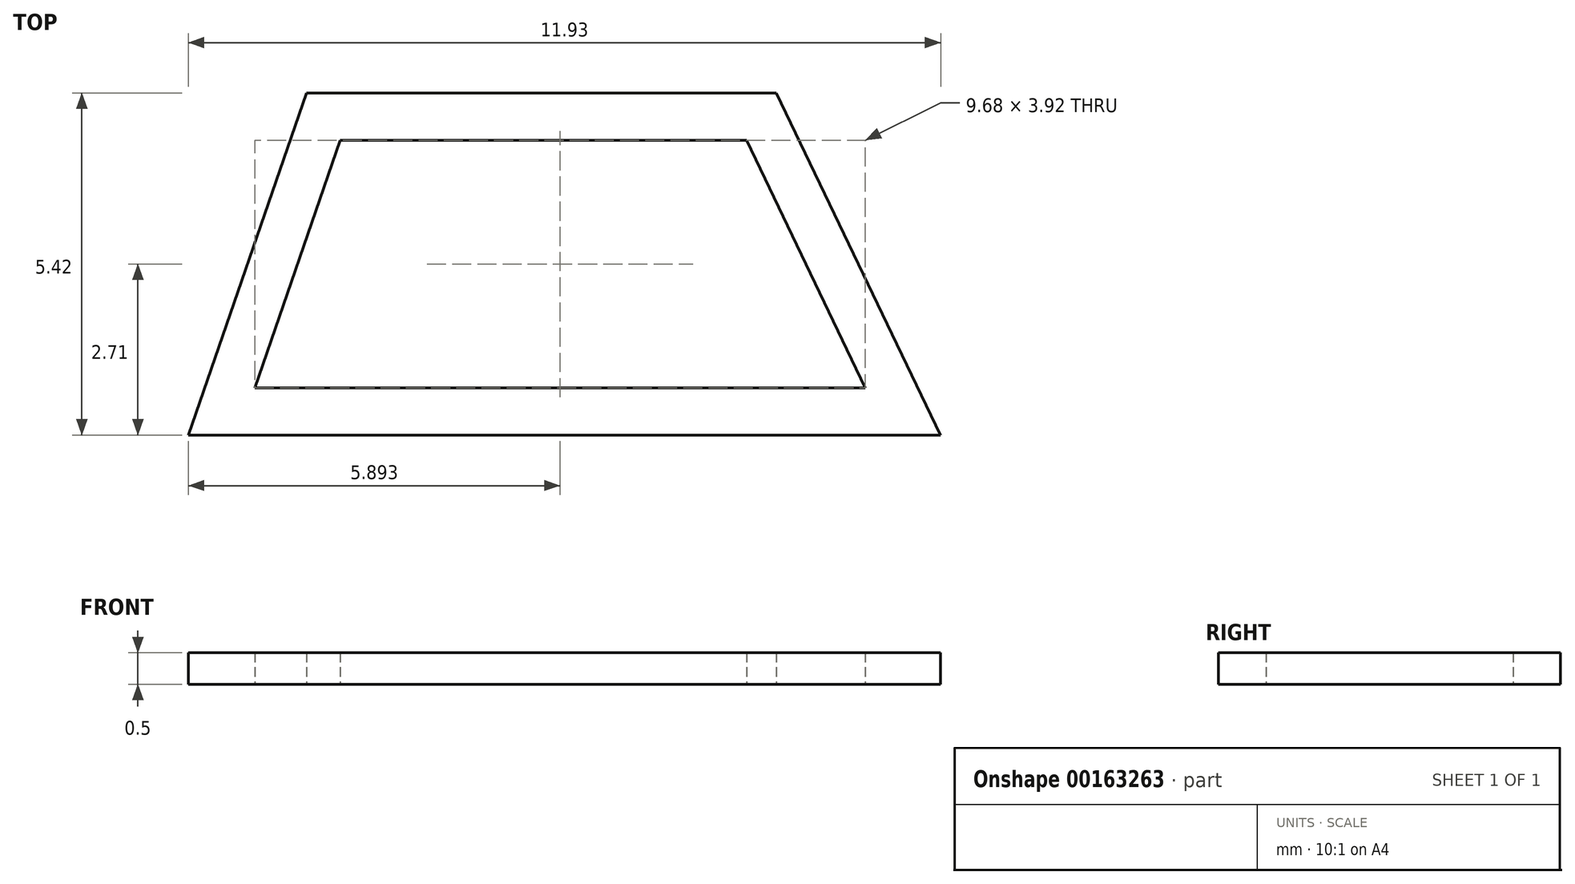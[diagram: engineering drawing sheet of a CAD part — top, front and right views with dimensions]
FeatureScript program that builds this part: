
annotation { "Feature Type Name" : "Feature", "Feature Type Description" : "" }
export const myFeature = defineFeature(function(context is Context, id is Id, definition is map)
    precondition{}
    {
        {
            var Q0;
            Q0=qCreatedBy(makeId("Top.planeOp"),FACE);
            var sketch = newSketch(context, id + "F0", { "sketchPlane" : qUnion([Q0])});
            skLineSegment(sketch, "E0", {"start": v(0, 0) * mm, "end": v(11.93, 0) * mm});
            skLineSegment(sketch, "E1", {"start": v(0, 0) * mm, "end": v(1.87, 5.42) * mm});
            skLineSegment(sketch, "E2", {"start": v(1.87, 5.42) * mm, "end": v(9.32, 5.42) * mm});
            skLineSegment(sketch, "E3", {"start": v(9.32, 5.42) * mm, "end": v(11.93, 0) * mm});
            skLineSegment(sketch, "E4", {"start": v(1.05, 0.75) * mm, "end": v(2.4, 4.67) * mm});
            skLineSegment(sketch, "E5", {"start": v(2.4, 4.67) * mm, "end": v(8.85, 4.67) * mm});
            skLineSegment(sketch, "E6", {"start": v(8.85, 4.67) * mm, "end": v(10.73, 0.75) * mm});
            skLineSegment(sketch, "E7", {"start": v(10.73, 0.75) * mm, "end": v(1.05, 0.75) * mm});
            skSolve(sketch);
        }
        {
            var Q0;
            Q0 = qSketchRegion(id + "F0", true);
            extrude(context, id + "F1", {"entities" : qUnion([Q0]), "depth" : .5 * mm});
        }
    });
